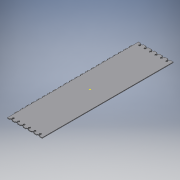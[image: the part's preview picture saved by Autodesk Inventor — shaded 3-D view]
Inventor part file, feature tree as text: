
AUTODESK INVENTOR PART (.ipt)
format: ipt  version: 2016 (Build 200138000, 138)  size: 450,048 bytes
history: native  units: in
note: dims shown in document units (in); Inventor stores cm internally (conversion verified against a paired STEP export)
features: sketch x11, extrude x10, pattern_linear x2, mirror x1
ambient origin geometry x8: Origin, YZ Plane, XZ Plane, XY Plane, X Axis, Y Axis, Z Axis, Center Point
bodies: Solid1 (feature_tree)
feature tree (24):
  extrude  "Extrusion1"  Depth=6.5in
  extrude  "Extrusion2"  Depth=0.5in
  extrude  "Extrusion3"  Depth=0.125in
  extrude  "Extrusion4"  Depth=0.14in
  extrude  "Extrusion5"  Depth=0.18in
  pattern_linear  "Rectangular Pattern1"  Spacing1=0.14in  [1 undecoded]
  sketch  "Sketch6"  dims[d12=0.25in d13=0.0in]
  mirror  "Mirror1"
  extrude  "Extrusion13"  Depth=0.18in
  extrude  "Extrusion14"  Depth=0.6in
  extrude  "Extrusion15"  Depth=1.126in TaperAngle=0.0deg
  extrude  "Extrusion16"  Depth=1.0in
  pattern_linear  "Rectangular Pattern3"  Count1=4  [1 undecoded]
  extrude  "Extrusion17"  Depth=1.126in
  sketch  "Sketch1"  dims[d0=24.125in d1=6.5in]
  sketch  "Sketch2"  dims[d2=0.125in d3=0.0in d4=0.5in]
  sketch  "Sketch3"  dims[d5=0.5in d6=0.125in]
  sketch  "Sketch4"  dims[d7=0.25in d8=0.0in d9=0.14in]
  sketch  "Sketch5"  dims[d10=0.2362in d11=0.18in]
  sketch  "Sketch18"  dims[d14=0.3125in]
  sketch  "Sketch19"  dims[d15=0.1094in]
  sketch  "Sketch20"  dims[d16=0.0in]
  sketch  "Sketch21"  dims[d17=0.0937in]
  sketch  "Sketch22"  dims[d18=0.25in d19=0.0in d20=0.14in d21=0.18in d22=0.6in d23=0.25in d24=0.0in d25=2.3622in d27=1.0in d120=1.5748in d121=1.5748in d122=5.0709in d123=0.9843in d124=0.3937in d125=0.0in d126=0.2165in d127=0.3937in d128=0.2165in d129=0.7874in d130=0.565in d131=0.565in d132=0.3937in d133=0.0in d134=0.125in d135=1.5in d136=0.18in d137=0.14in d138=0.3937in d139=0.0in d140=0.125in d141=0.18in d142=0.5in d143=0.181in d144=0.14in d145=0.3937in d146=0.0in d147=8.2677in d149=1.0in d150=0.125in d152=0.3937in d153=0.0in d154=1.126in]
note: 2 required parameter values undecoded (feature->parameter linkage not recoverable at this tier; creation-order binding heuristic only, values carry confidence <= 0.55)
